# Revit family: IS_Ipalyss_E1394_BIM_DE
name_source: partatom
category: Plumbing Fixtures
revit_build: Autodesk Revit MEP 2015 (Build: 20140606_1530(x64)
units: mm (PartAtom-declared; Revit-internal decimal feet)

## types (1)
- E139401 - IPALYSS - Vessel Basin 550 mm
    BIMobject category = Basins
    BOSUseNativeGeometries = 1
    Brand url = http://www.idealstandard.co.uk
    Description = E139401 IPALYSS vessel basin 550x380mm, no taphole, with overflow
    DrainSize = 42 mm  [stored 0.137795 ft]
    EAN code = https://5017830527947
    Edition number = 1
    IfcExportAs = WASHHANDBASIN
    IfcExportType = WASHBASIN
    Installation instructions = http://www.idealspec.co.uk
    Manufacturer name = Ideal Standard
    ManufacturerURL = www.idealstandard.com
    Material = Vitreous china
    Material main = Ceramics
    Model = E139401
    ModelNumber = E139401
    Name = IPALYSS vessel basin 550x380mm, no taphole, with overflow
    Nominal height = 145
    Nominal width = 550
    NominalDepth = 0 mm  [stored 0 ft]
    NominalHeight = 145 mm  [stored 0.475722 ft]
    NominalLength = 0 mm  [stored 0 ft]
    NominalWidth = 550 mm  [stored 1.80446 ft]
    Product Guid = 241e9c8b-6286-4d91-b32b-af02a35a678e
    Product SKU = E1394
    Product data url = https://bimobject.com
    Product family = IPALYSS
    Product group = Basin
    Product name = Ipalyss Vessel Basin 55X38 White Rect Of
    Product url = http://www.idealspec.co.uk
    ProductInformation = www.idealstandard.de/produkte
    QR code = http://bimobject.com
    Shape = Sculptured
    Size = 550x380
    Space = Internal
    SpareParts = www.idealstandard.de/ersatzteile
    Technical description = http://www.idealspec.co.uk
    URL = www.idealstandard.com
    Uniclass 2015 Code = Pr_40_20_98
    Uniclass 2015 Name = Wash basins, sinks and troughs
    Uniclass2015Code = Pr_40_20_98
    Version = 1
    VolumeUnits = Litres
    WarrantyDurationUnit = year
    WashHandBasinType = Hand Rinse
    Weight Net (Kg) = 9.1

note: [stored X ft] marks values corroborated as IEEE doubles in the binary element streams (Revit-internal decimal feet)

## geometry (parser evidence)
native form markers: Blend x4, Sweep x1
no freeform markers — native parametric forms only
